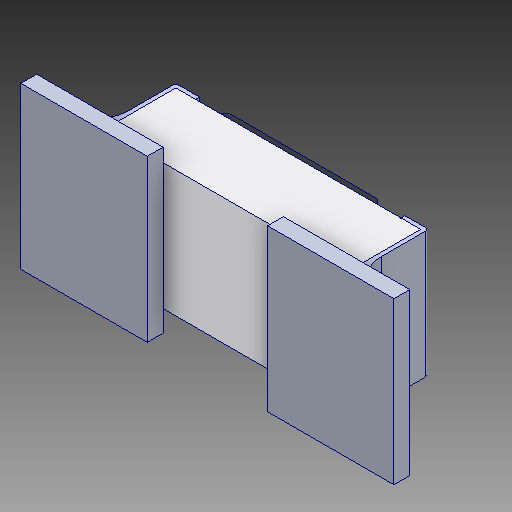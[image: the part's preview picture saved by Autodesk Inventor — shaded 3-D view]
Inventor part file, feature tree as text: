
AUTODESK INVENTOR PART (.ipt)
format: ipt  version: 2018 (Build 220112000, 112)  size: 249,856 bytes
history: native  units: mm
features: other x2, fillet x2
ambient origin geometry x8: Origin, YZ Plane, XZ Plane, XY Plane, X Axis, Y Axis, Z Axis, Center Point
bodies: Volumenkörper1 (feature_tree), Volumenkörper2 (feature_tree), Volumenkörper3 (feature_tree), Volumenkörper4 (feature_tree)
feature tree (4):
  other  "Boss-Extrude1"
  other  "Boss-Extrude4"
  fillet  "Fillet6"  [1 undecoded]
  fillet  "Fillet5"  [1 undecoded]
note: 2 required parameter values undecoded (feature->parameter linkage not recoverable at this tier; creation-order binding heuristic only, values carry confidence <= 0.55)
